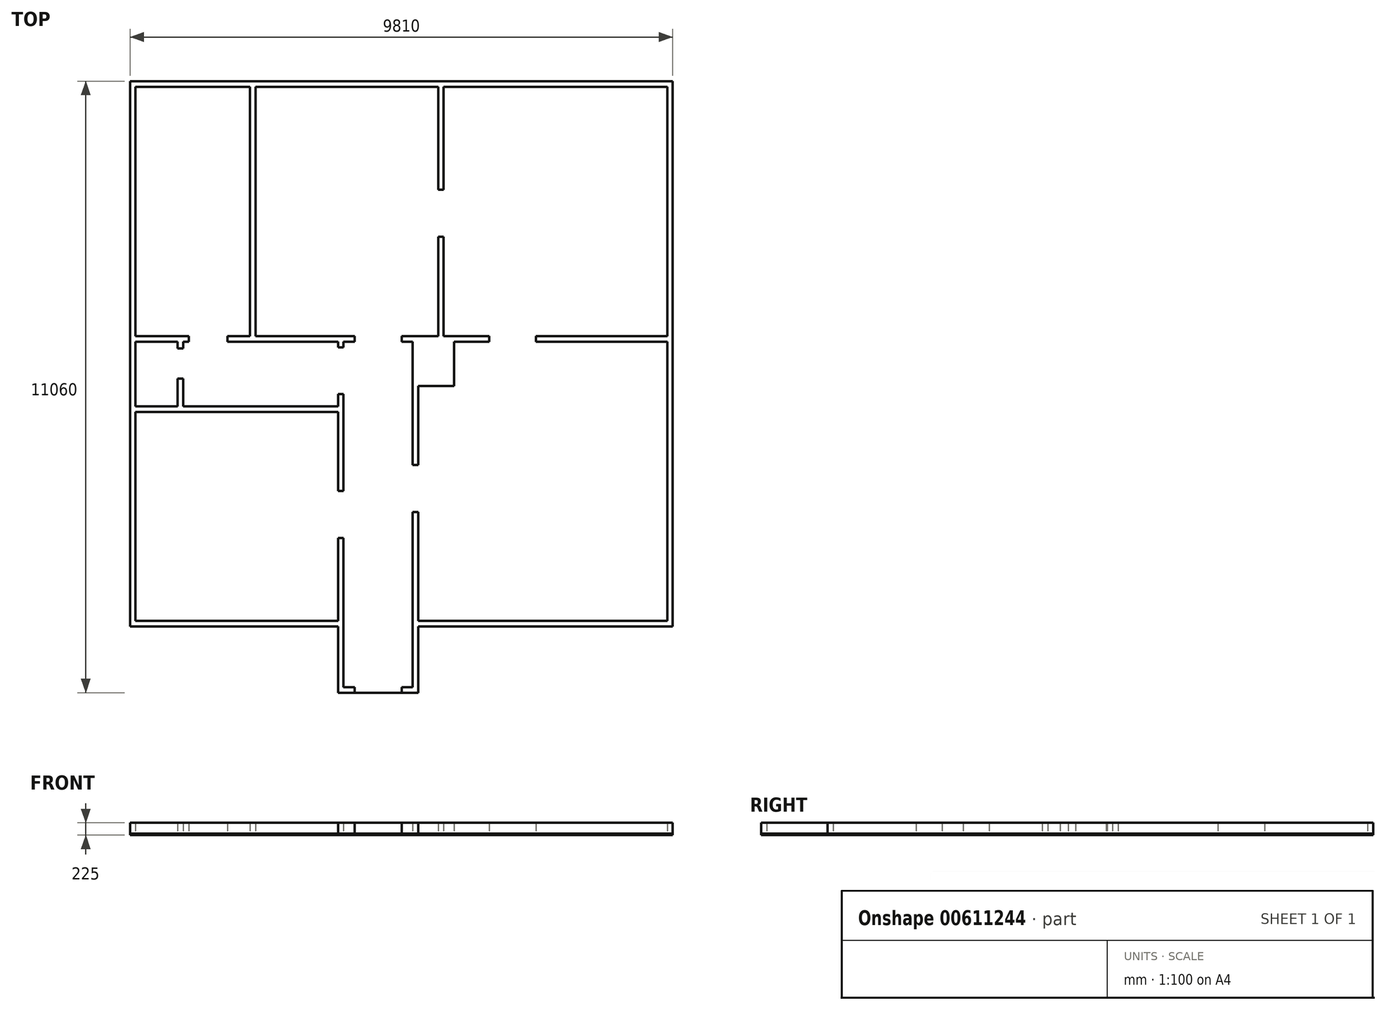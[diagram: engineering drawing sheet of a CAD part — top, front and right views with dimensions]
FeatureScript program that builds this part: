
annotation { "Feature Type Name" : "Feature", "Feature Type Description" : "" }
export const myFeature = defineFeature(function(context is Context, id is Id, definition is map)
    precondition{}
    {
        {
            var Q0;
            Q0=qCreatedBy(makeId("Top.planeOp"),FACE);
            var sketch = newSketch(context, id + "F0", { "sketchPlane" : qUnion([Q0])});
            skLineSegment(sketch, "E0", {"start": v(300, 0) * mm, "end": v(300, 100) * mm});
            skLineSegment(sketch, "E1", {"start": v(300, 100) * mm, "end": v(100, 100) * mm});
            skLineSegment(sketch, "E2", {"start": v(100, 100) * mm, "end": v(100, 184.21) * mm});
            skLineSegment(sketch, "E3", {"start": v(0, 0) * mm, "end": v(0, 184.21) * mm});
            skLineSegment(sketch, "E4", {"start": v(300, 0) * mm, "end": v(0, 0) * mm});
            skLineSegment(sketch, "E5", {"start": v(0, 184.21) * mm, "end": v(0, 1200) * mm});
            skLineSegment(sketch, "E6", {"start": v(0, 1200) * mm, "end": v(-3760, 1200) * mm});
            skLineSegment(sketch, "E7", {"start": v(-3760, 1200) * mm, "end": v(-3760, 11060) * mm});
            skLineSegment(sketch, "E8", {"start": v(-3760, 11060) * mm, "end": v(6050, 11060) * mm});
            skLineSegment(sketch, "E9", {"start": v(6050, 11060) * mm, "end": v(6050, 1200) * mm});
            skLineSegment(sketch, "E10", {"start": v(6050, 1200) * mm, "end": v(1450, 1200) * mm});
            skLineSegment(sketch, "E11", {"start": v(1450, 1200) * mm, "end": v(1450, 0) * mm});
            skLineSegment(sketch, "E12", {"start": v(1450, 0) * mm, "end": v(1150, 0) * mm});
            skLineSegment(sketch, "E13", {"start": v(1150, 0) * mm, "end": v(1150, 100) * mm});
            skLineSegment(sketch, "E14", {"start": v(1150, 100) * mm, "end": v(1350, 100) * mm});
            skLineSegment(sketch, "E15", {"start": v(1350, 100) * mm, "end": v(1350, 3270) * mm});
            skLineSegment(sketch, "E16", {"start": v(100, 184.21) * mm, "end": v(100, 2800) * mm});
            skLineSegment(sketch, "E17", {"start": v(100, 2800) * mm, "end": v(0, 2800) * mm});
            skLineSegment(sketch, "E18", {"start": v(0, 2800) * mm, "end": v(0, 1300) * mm});
            skLineSegment(sketch, "E19", {"start": v(0, 1300) * mm, "end": v(-3660, 1300) * mm});
            skLineSegment(sketch, "E20", {"start": v(-3660, 1300) * mm, "end": v(-3660, 5080) * mm});
            skLineSegment(sketch, "E21", {"start": v(-3660, 5080) * mm, "end": v(0, 5080) * mm});
            skLineSegment(sketch, "E22", {"start": v(0, 5080) * mm, "end": v(0, 3650) * mm});
            skLineSegment(sketch, "E23", {"start": v(0, 3650) * mm, "end": v(100, 3650) * mm});
            skLineSegment(sketch, "E24", {"start": v(100, 3650) * mm, "end": v(100, 5400) * mm});
            skLineSegment(sketch, "E25", {"start": v(100, 5400) * mm, "end": v(0, 5400) * mm});
            skLineSegment(sketch, "E26", {"start": v(0, 5400) * mm, "end": v(0, 5180) * mm});
            skLineSegment(sketch, "E27", {"start": v(0, 5180) * mm, "end": v(-2800, 5180) * mm});
            skLineSegment(sketch, "E28", {"start": v(-2800, 5180) * mm, "end": v(-2800, 5680) * mm});
            skLineSegment(sketch, "E29", {"start": v(-2800, 5680) * mm, "end": v(-2900, 5680) * mm});
            skLineSegment(sketch, "E30", {"start": v(-2900, 5680) * mm, "end": v(-2900, 5180) * mm});
            skLineSegment(sketch, "E31", {"start": v(-2900, 5180) * mm, "end": v(-3660, 5180) * mm});
            skLineSegment(sketch, "E32", {"start": v(-3660, 5180) * mm, "end": v(-3660, 6350) * mm});
            skLineSegment(sketch, "E33", {"start": v(-3660, 6350) * mm, "end": v(-2900, 6350) * mm});
            skLineSegment(sketch, "E34", {"start": v(-2900, 6350) * mm, "end": v(-2900, 6230) * mm});
            skLineSegment(sketch, "E35", {"start": v(-2900, 6230) * mm, "end": v(-2800, 6230) * mm});
            skLineSegment(sketch, "E36", {"start": v(-2800, 6230) * mm, "end": v(-2800, 6350) * mm});
            skLineSegment(sketch, "E37", {"start": v(-2800, 6350) * mm, "end": v(-2700, 6350) * mm});
            skLineSegment(sketch, "E38", {"start": v(-2700, 6350) * mm, "end": v(-2700, 6450) * mm});
            skLineSegment(sketch, "E39", {"start": v(-2700, 6450) * mm, "end": v(-3660, 6450) * mm});
            skLineSegment(sketch, "E40", {"start": v(-3660, 6450) * mm, "end": v(-3660, 10960) * mm});
            skLineSegment(sketch, "E41", {"start": v(-3660, 10960) * mm, "end": v(-1590, 10960) * mm});
            skLineSegment(sketch, "E42", {"start": v(-1590, 10960) * mm, "end": v(-1590, 6450) * mm});
            skLineSegment(sketch, "E43", {"start": v(-1590, 6450) * mm, "end": v(-2000, 6450) * mm});
            skLineSegment(sketch, "E44", {"start": v(-2000, 6450) * mm, "end": v(-2000, 6350) * mm});
            skLineSegment(sketch, "E45", {"start": v(-2000, 6350) * mm, "end": v(0, 6350) * mm});
            skLineSegment(sketch, "E46", {"start": v(0, 6350) * mm, "end": v(0, 6250) * mm});
            skLineSegment(sketch, "E47", {"start": v(0, 6250) * mm, "end": v(100, 6250) * mm});
            skLineSegment(sketch, "E48", {"start": v(100, 6250) * mm, "end": v(100, 6350) * mm});
            skLineSegment(sketch, "E49", {"start": v(100, 6350) * mm, "end": v(300, 6350) * mm});
            skLineSegment(sketch, "E50", {"start": v(300, 6350) * mm, "end": v(300, 6450) * mm});
            skLineSegment(sketch, "E51", {"start": v(300, 6450) * mm, "end": v(-1490, 6450) * mm});
            skLineSegment(sketch, "E52", {"start": v(-1490, 6450) * mm, "end": v(-1490, 10960) * mm});
            skPoint(sketch, "E53.endSnap0", {"position": v(1145, 11060) * mm});
            skLineSegment(sketch, "E54", {"start": v(1150, 6350) * mm, "end": v(1150, 6450) * mm});
            skLineSegment(sketch, "E55", {"start": v(1150, 6450) * mm, "end": v(1810, 6450) * mm});
            skLineSegment(sketch, "E56", {"start": v(1810, 6450) * mm, "end": v(1810, 8250) * mm});
            skLineSegment(sketch, "E57", {"start": v(1810, 8250) * mm, "end": v(1910, 8250) * mm});
            skLineSegment(sketch, "E58", {"start": v(1910, 8250) * mm, "end": v(1910, 6450) * mm});
            skLineSegment(sketch, "E59", {"start": v(1910, 6450) * mm, "end": v(2730, 6450) * mm});
            skLineSegment(sketch, "E60", {"start": v(2730, 6450) * mm, "end": v(2730, 6350) * mm});
            skLineSegment(sketch, "E61", {"start": v(2730, 6350) * mm, "end": v(1450, 6350) * mm});
            skLineSegment(sketch, "E62", {"start": v(1450, 6350) * mm, "end": v(1450, 4120) * mm});
            skLineSegment(sketch, "E63", {"start": v(1450, 4120) * mm, "end": v(1350, 4120) * mm});
            skLineSegment(sketch, "E64", {"start": v(1350, 4120) * mm, "end": v(1350, 6350) * mm});
            skLineSegment(sketch, "E65", {"start": v(1350, 6350) * mm, "end": v(1150, 6350) * mm});
            skLineSegment(sketch, "E66", {"start": v(1350, 3270) * mm, "end": v(1450, 3270) * mm});
            skLineSegment(sketch, "E67", {"start": v(1450, 3270) * mm, "end": v(1450, 1300) * mm});
            skLineSegment(sketch, "E68", {"start": v(1450, 1300) * mm, "end": v(5950, 1300) * mm});
            skLineSegment(sketch, "E69", {"start": v(5950, 1300) * mm, "end": v(5950, 6350) * mm});
            skLineSegment(sketch, "E70", {"start": v(5950, 6350) * mm, "end": v(3580, 6350) * mm});
            skLineSegment(sketch, "E71", {"start": v(3580, 6350) * mm, "end": v(3580, 6450) * mm});
            skLineSegment(sketch, "E72", {"start": v(3580, 6450) * mm, "end": v(5950, 6450) * mm});
            skLineSegment(sketch, "E73", {"start": v(5950, 6450) * mm, "end": v(5950, 10960) * mm});
            skLineSegment(sketch, "E74", {"start": v(5950, 10960) * mm, "end": v(1910, 10960) * mm});
            skLineSegment(sketch, "E75", {"start": v(1910, 10960) * mm, "end": v(1910, 9100) * mm});
            skLineSegment(sketch, "E76", {"start": v(1910, 9100) * mm, "end": v(1810, 9100) * mm});
            skLineSegment(sketch, "E77", {"start": v(1810, 9100) * mm, "end": v(1810, 10960) * mm});
            skLineSegment(sketch, "E78", {"start": v(1810, 10960) * mm, "end": v(-1490, 10960) * mm});
            skLineSegment(sketch, "E79", {"start": v(1450, 5550) * mm, "end": v(2100, 5550) * mm});
            skLineSegment(sketch, "E80", {"start": v(2100, 5550) * mm, "end": v(2100, 6350) * mm});
            skSolve(sketch);
        }
        {
            var Q0;
            Q0=qCreatedBy(makeId("Top.planeOp"),FACE);
            var sketch = newSketch(context, id + "F1", { "sketchPlane" : qUnion([Q0])});
            skLineSegment(sketch, "E81.bottom", {"start": v(-3760, 11060) * mm, "end": v(6050, 11060) * mm});
            skLineSegment(sketch, "E81.top", {"start": v(-3760, 1200) * mm, "end": v(0, 1200) * mm});
            skLineSegment(sketch, "E81.left", {"start": v(-3760, 11060) * mm, "end": v(-3760, 1200) * mm});
            skLineSegment(sketch, "E81.right", {"start": v(6050, 11060) * mm, "end": v(6050, 1200) * mm});
            skLineSegment(sketch, "E82.bottom", {"start": v(0, 0) * mm, "end": v(1450, 0) * mm});
            skLineSegment(sketch, "E82.left", {"start": v(0, 0) * mm, "end": v(0, 1200) * mm});
            skLineSegment(sketch, "E82.right", {"start": v(1450, 0) * mm, "end": v(1450, 1200) * mm});
            skLineSegment(sketch, "E83.trimOffspring", {"start": v(1450, 1200) * mm, "end": v(6050, 1200) * mm});
            skSolve(sketch);
        }
        {
            var Q0;
            Q0 = qSketchRegion(id + "F1", true);
            extrude(context, id + "F2", {"entities" : qUnion([Q0]), "oppositeDirection" : true, "depth" : 25 * mm, "offsetDistance" : 25 * mm});
        }
        {
            var Q0;
            Q0 = qSketchRegion(id + "F0", true);
            extrude(context, id + "F3", {"entities" : qUnion([Q0]), "depth" : 200 * mm, "offsetDistance" : 25 * mm});
        }
    });
